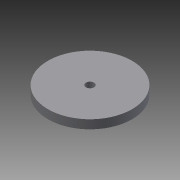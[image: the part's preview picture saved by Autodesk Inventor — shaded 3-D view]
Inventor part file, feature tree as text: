
AUTODESK INVENTOR PART (.ipt)
format: ipt  version: 2013 SP1 (Build 170176100, 176)  size: 72,192 bytes
history: native  units: mm
features: extrude x1, sketch x1
ambient origin geometry x8: Origin, YZ Plane, XZ Plane, XY Plane, X Axis, Y Axis, Z Axis, Center Point
bodies: Solid1 (feature_tree)
feature tree (2):
  extrude  "Extrusion1"  Depth=2.8mm
  sketch  "Sketch1"  dims[d0=29.0mm d3=2.8mm d4=3.0mm d5=0.0mm]
